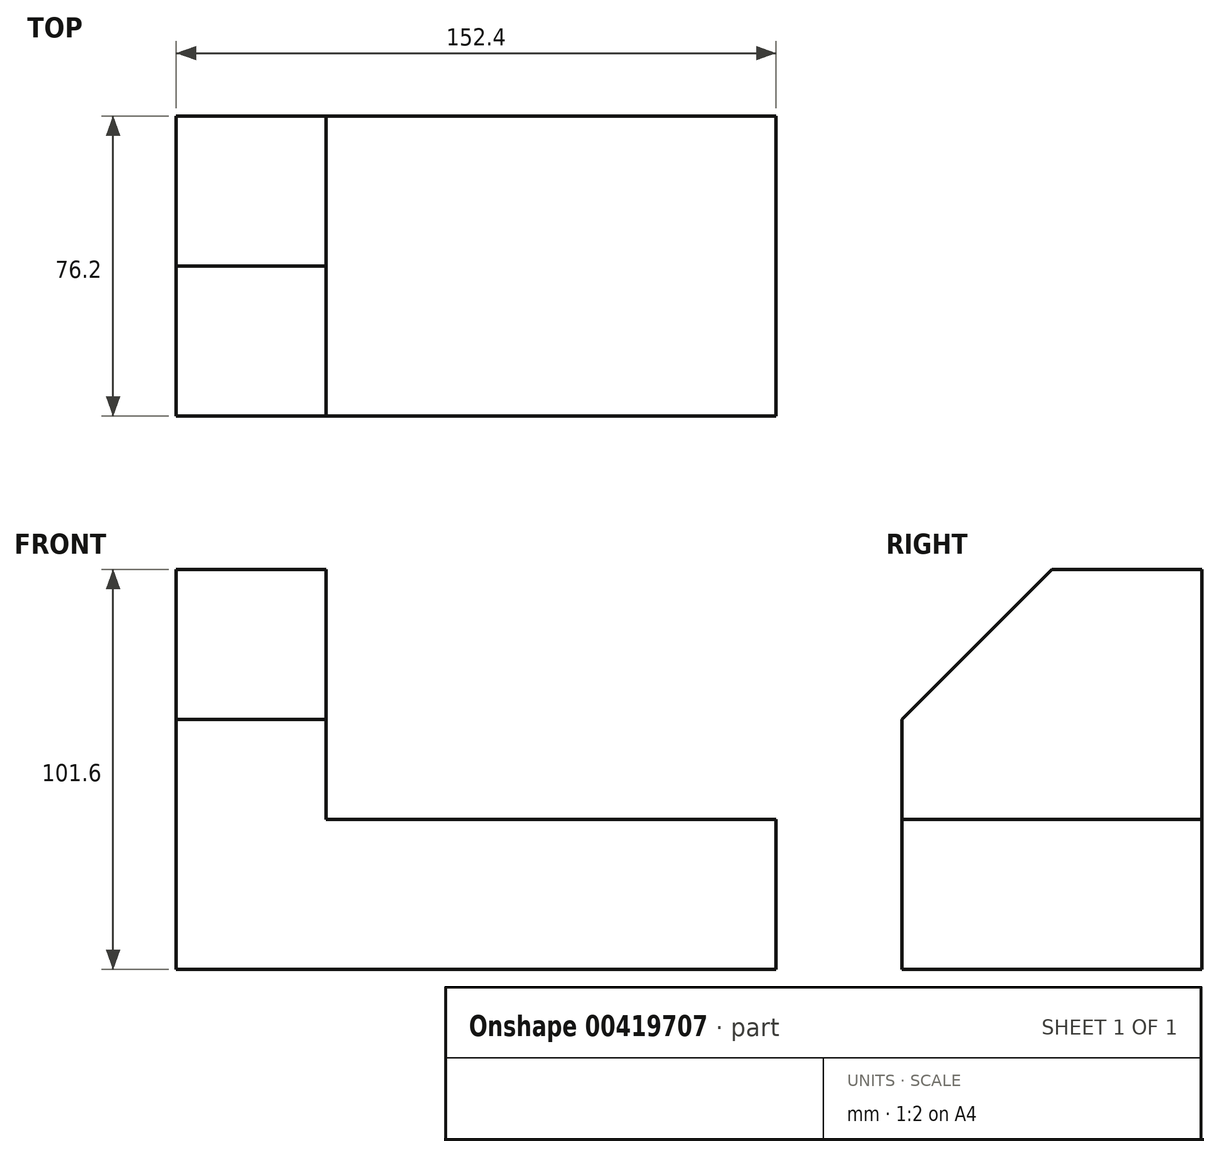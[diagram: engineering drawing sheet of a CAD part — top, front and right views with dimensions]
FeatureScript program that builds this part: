
annotation { "Feature Type Name" : "Feature", "Feature Type Description" : "" }
export const myFeature = defineFeature(function(context is Context, id is Id, definition is map)
    precondition{}
    {
        {
            var Q0;
            Q0=qCreatedBy(makeId("Front.planeOp"),FACE);
            var sketch = newSketch(context, id + "F0", { "sketchPlane" : qUnion([Q0])});
            skLineSegment(sketch, "E0", {"start": v(0, 0) * mm, "end": v(152.4, 0) * mm});
            skLineSegment(sketch, "E1", {"start": v(152.4, 0) * mm, "end": v(152.4, 38.1) * mm});
            skLineSegment(sketch, "E2", {"start": v(152.4, 38.1) * mm, "end": v(38.1, 38.1) * mm});
            skLineSegment(sketch, "E3", {"start": v(38.1, 38.1) * mm, "end": v(38.1, 101.6) * mm});
            skLineSegment(sketch, "E4", {"start": v(38.1, 101.6) * mm, "end": v(0, 101.6) * mm});
            skLineSegment(sketch, "E5", {"start": v(0, 101.6) * mm, "end": v(0, 0) * mm});
            skSolve(sketch);
        }
        {
            var Q0;
            Q0 = qSketchRegion(id + "F0", true);
            extrude(context, id + "F1", {"entities" : qUnion([Q0]), "depth" : 76.2 * mm});
        }
        {
            var Q0;
            Q0=makeQuery(id+"F1.opExtrude","SWEPT_FACE",FACE,{"disambiguationData":[OSD([sQuery(id+"F0.wireOp",EDGE,"E3")])]});
            var sketch = newSketch(context, id + "F2", { "sketchPlane" : qUnion([Q0])});
            skLineSegment(sketch, "E6", {"start": v(-38.1, 101.6) * mm, "end": v(-76.2, 63.5) * mm});
            skLineSegment(sketch, "E7", {"start": v(-76.2, 101.6) * mm, "end": v(-76.2, 63.5) * mm});
            skSolve(sketch);
        }
        {
            var Q0;
            {var subQ0=sQuery(id+"F2.wireOp",EDGE,"E6");Q0=makeQuery(id+"F2.imprint","IMPRINT",FACE,{"disambiguationData":[TD([[makeQuery(id+"F2.imprint","IMPRINT",EDGE,{"derivedFrom":subQ0}),-1.0]])]});}
            extrude(context, id + "F3", {"entities" : qUnion([Q0]), "operationType" : NewBodyOperationType.REMOVE, "oppositeDirection" : true, "depth" : 45.72 * mm});
        }
    });
